# Revit family: Electronics_Wall-Stations_Biamp_Vocia_Auxiliary-Microphone_VAM-1__
name_source: partatom
category: Communication Devices
units: mm (PartAtom-declared; Revit-internal decimal feet)

## family parameters
Cut with Voids When Loaded = No
Host = Face
Maintain Annotation Orientation = No
OmniClass Number = 23.85.10.11.14
OmniClass Title = Audio Equipment
Part Type = Normal
Room Calculation Point = No
Round Connector Dimension = Use Diameter
Shared = No

## types (1)
- VAM-1
    Altitude = 0-10,000 ft (0-3000m) MSL
    Apparent Load = 0 VA
    Compliance = CE marked (Europe) RoHS Directive (Europe)
    Connector Description = Power (from host): RJ45; 12V DC, 50 mA
    Default Elevation = 4' - 0"
    Depth = 0' - 2 3/16"
    Description = Vocia® VAM-1 Auxiliary Microphone
    Effective Input Headroom = 30dB
    Frequency Response = 20Hz~10kHz: +0, -1dB
    Headroom = > 25dB
    Height = 0' - 5 13/32"
    Housing Material = Biamp - Plastic - Black
    Humidity = 0-95% relative humidity (non-condensing)
    Input Common Mode Rejection Ratio = 200Hz~20kHz: >50dB
    Input Impedance = 3 kohm
    Manufacturer = Biamp
    Max Cable Length = 100' - 0"
    Max Power Consumption = 0 W
    Maximum Input = 125dB SPL
    Microphone Cord Length = 4' - 0"
    Microphone Type = Dynamic microphone with dual transducer un-monitored)
    Model = Vocia VAM-1
    Network Connection = RJ45 with shielded Ethernet (CAT5, CAT5e, CAT6 or CAT7
    Nominal Input Level = -45dBu
    Nominal Output Level = -10dBu
    Number of Poles = 1
    Power = From host: 12V DC, 50 mA
    Power Factor = 1
    Product Documentation Link = https://downloads.biamp.com
    Product Page URL = https://www.biamp.com
    Product data url = https://www.bimobject.com
    SNR = 20Hz ~ 20kHz, 35dB Gain, 150 ohm: > 65dB
    System Headroom = 18dB
    THD+N = 20Hz~10kHz: <0.08%; 20Hz~10kHz, at -35dBu In: <0.08%
    Temperature Range = 23 - 104° F (-5 – 40° C)
    URL = https://www.biamp.com
    Voltage = 24 V
    Weight = 0.55 lbf
    Width = 0' - 2 1/2"

## geometry (parser evidence)
native form markers: Sweep x5
no freeform markers — native parametric forms only
